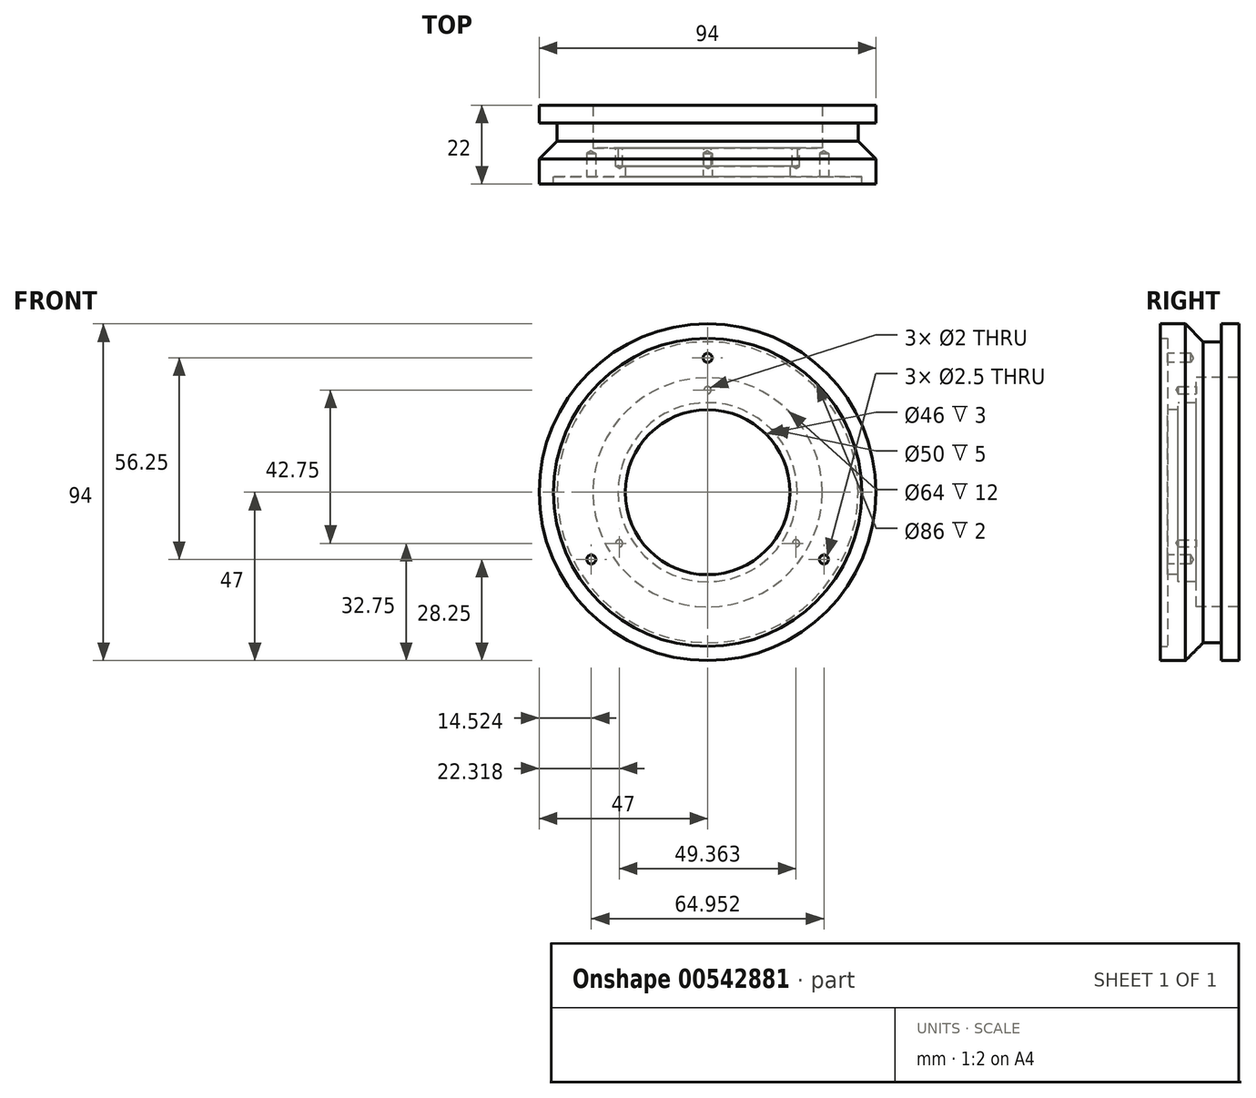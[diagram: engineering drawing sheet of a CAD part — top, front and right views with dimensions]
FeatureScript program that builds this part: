
annotation { "Feature Type Name" : "Feature", "Feature Type Description" : "" }
export const myFeature = defineFeature(function(context is Context, id is Id, definition is map)
    precondition{}
    {
        {
            var Q0;
            Q0=qCreatedBy(makeId("Right.planeOp"),FACE);
            var sketch = newSketch(context, id + "F0", { "sketchPlane" : qUnion([Q0])});
            skLineSegment(sketch, "E0", {"start": v(0, 47) * mm, "end": v(0, 23) * mm});
            skLineSegment(sketch, "E1", {"start": v(0, 23) * mm, "end": v(3, 23) * mm});
            skLineSegment(sketch, "E2", {"start": v(3, 23) * mm, "end": v(3, 25) * mm});
            skLineSegment(sketch, "E3", {"start": v(3, 25) * mm, "end": v(8, 25) * mm});
            skLineSegment(sketch, "E4", {"start": v(8, 25) * mm, "end": v(8, 32) * mm});
            skLineSegment(sketch, "E5", {"start": v(8, 32) * mm, "end": v(20, 32) * mm});
            skLineSegment(sketch, "E6", {"start": v(20, 32) * mm, "end": v(20, 47) * mm});
            skLineSegment(sketch, "E7", {"start": v(20, 47) * mm, "end": v(15, 47) * mm});
            skLineSegment(sketch, "E8", {"start": v(15, 47) * mm, "end": v(15, 42) * mm});
            skLineSegment(sketch, "E9", {"start": v(15, 42) * mm, "end": v(10, 42) * mm});
            skLineSegment(sketch, "E10", {"start": v(10, 42) * mm, "end": v(5, 47) * mm});
            skLineSegment(sketch, "E11", {"start": v(5, 47) * mm, "end": v(0, 47) * mm});
            skLineSegment(sketch, "E12", {"start": v(0, 0) * mm, "end": v(26.07, 0) * mm, "construction": true});
            skSolve(sketch);
        }
        {
            var Q0;
            Q0=makeQuery(id+"F0.imprint","IMPRINT",FACE,{"disambiguationData":[TD([[makeQuery(id+"F0.imprint","IMPRINT",EDGE,{"derivedFrom":sQuery(id+"F0.wireOp",EDGE,"E0")}),1.0]])]});
            var Q1;
            Q1=sQuery(id+"F0.wireOp",EDGE,"E12");
            revolve(context, id + "F1", {"entities" : qUnion([Q0]), "axis" : qUnion([Q1]), "revolveType" : RevolveType.FULL});
        }
        {
            var Q0;
            Q0=makeQuery(id+"F1.opRevolve","SWEPT_FACE",FACE,{"disambiguationData":[OSD([sQuery(id+"F0.wireOp",EDGE,"E4")])]});
            var sketch = newSketch(context, id + "F2", { "sketchPlane" : qUnion([Q0])});
            skLineSegment(sketch, "E13", {"start": v(0, 32) * mm, "end": v(0, 25) * mm, "construction": true});
            skPoint(sketch, "E14", {"position": v(0, 28.5) * mm});
            skPoint(sketch, "E15.1.0", {"position": v(-24.68, -14.25) * mm});
            skPoint(sketch, "E15.2.0", {"position": v(24.68, -14.25) * mm});
            skPoint(sketch, "E15.center", {"position": v(0, 0) * mm});
            skSolve(sketch);
        }
        {
            var Q0;
            Q0=sQuery(id+"F2.wireOp",VERTEX,"E14");
            var Q1;
            Q1=sQuery(id+"F2.wireOp",VERTEX,"E15.2.0");
            var Q2;
            Q2=sQuery(id+"F2.wireOp",VERTEX,"E15.1.0");
            var Q3;
            Q3=makeQuery(id+"F1.opRevolve","SWEPT_BODY",BODY,{"disambiguationData":[OSD([sQuery(id+"F0.wireOp",EDGE,"E0"),sQuery(id+"F0.wireOp",EDGE,"E1"),sQuery(id+"F0.wireOp",EDGE,"E2"),sQuery(id+"F0.wireOp",EDGE,"E3"),sQuery(id+"F0.wireOp",EDGE,"E4"),sQuery(id+"F0.wireOp",EDGE,"E5"),sQuery(id+"F0.wireOp",EDGE,"E6"),sQuery(id+"F0.wireOp",EDGE,"E7"),sQuery(id+"F0.wireOp",EDGE,"E8"),sQuery(id+"F0.wireOp",EDGE,"E9"),sQuery(id+"F0.wireOp",EDGE,"E10"),sQuery(id+"F0.wireOp",EDGE,"E11")])]});
            hole(context, id + "F3", {"style" : HoleStyle.SIMPLE, "endStyle" : HoleEndStyle.BLIND, "holeDiameter" : 2 * mm, "majorDiameter" : 3 * mm, "holeDepth" : 5 * mm, "isTappedThrough" : true, "tappedDepth" : 6.5 * mm, "tapClearance" : 3, "locations" : qUnion([Q0, Q1, Q2]), "scope" : qUnion([Q3])});
        }
        {
            var Q0;
            Q0=qCreatedBy(makeId("Right.planeOp"),FACE);
            var sketch = newSketch(context, id + "F4", { "sketchPlane" : qUnion([Q0])});
            skLineSegment(sketch, "E16", {"start": v(0, 47) * mm, "end": v(0, 43) * mm});
            skLineSegment(sketch, "E17", {"start": v(0, 43) * mm, "end": v(-2, 43) * mm});
            skLineSegment(sketch, "E18", {"start": v(-2, 43) * mm, "end": v(-2, 47) * mm});
            skLineSegment(sketch, "E19", {"start": v(-2, 47) * mm, "end": v(0, 47) * mm});
            skLineSegment(sketch, "E20", {"start": v(0, 0) * mm, "end": v(-15.8, 0) * mm, "construction": true});
            skSolve(sketch);
        }
        {
            var Q0;
            Q0=makeQuery(id+"F4.imprint","IMPRINT",FACE,{"disambiguationData":[TD([[makeQuery(id+"F4.imprint","IMPRINT",EDGE,{"derivedFrom":sQuery(id+"F4.wireOp",EDGE,"E16")}),-1.0]])]});
            var Q1;
            Q1=sQuery(id+"F4.wireOp",EDGE,"E20");
            revolve(context, id + "F5", {"operationType" : NewBodyOperationType.ADD, "entities" : qUnion([Q0]), "axis" : qUnion([Q1]), "revolveType" : RevolveType.FULL});
        }
        {
            var Q0;
            Q0=makeQuery(id+"F1.opRevolve","SWEPT_FACE",FACE,{"disambiguationData":[OSD([sQuery(id+"F0.wireOp",EDGE,"E0")])]});
            var sketch = newSketch(context, id + "F6", { "sketchPlane" : qUnion([Q0])});
            skCircle(sketch, "E21.0", {"center": v(0, 0) * mm, "radius": 32 * mm});
            skLineSegment(sketch, "E22", {"start": v(0, 32) * mm, "end": v(0, 43) * mm, "construction": true});
            skPoint(sketch, "E23", {"position": v(0, 37.5) * mm});
            skPoint(sketch, "E24.1.0", {"position": v(-32.48, -18.75) * mm});
            skPoint(sketch, "E24.2.0", {"position": v(32.48, -18.75) * mm});
            skSolve(sketch);
        }
        {
            var Q0;
            Q0=sQuery(id+"F6.wireOp",VERTEX,"E23");
            var Q1;
            Q1=sQuery(id+"F6.wireOp",VERTEX,"E24.2.0");
            var Q2;
            Q2=sQuery(id+"F6.wireOp",VERTEX,"E24.1.0");
            var Q3;
            Q3=makeQuery(id+"F1.opRevolve","SWEPT_BODY",BODY,{"disambiguationData":[OSD([sQuery(id+"F0.wireOp",EDGE,"E0"),sQuery(id+"F0.wireOp",EDGE,"E1"),sQuery(id+"F0.wireOp",EDGE,"E2"),sQuery(id+"F0.wireOp",EDGE,"E3"),sQuery(id+"F0.wireOp",EDGE,"E4"),sQuery(id+"F0.wireOp",EDGE,"E5"),sQuery(id+"F0.wireOp",EDGE,"E6"),sQuery(id+"F0.wireOp",EDGE,"E7"),sQuery(id+"F0.wireOp",EDGE,"E8"),sQuery(id+"F0.wireOp",EDGE,"E9"),sQuery(id+"F0.wireOp",EDGE,"E10"),sQuery(id+"F0.wireOp",EDGE,"E11")])]});
            hole(context, id + "F7", {"style" : HoleStyle.SIMPLE, "endStyle" : HoleEndStyle.BLIND, "standardTappedOrClearance" : lookupTablePath({ "standard" : "ISO", "engagement" : "75%", "pitch" : "0.5 mm", "size" : "M3", "type" : "Tapped" }), "standardBlindInLast" : lookupTablePath({ "standard" : "ISO", "engagement" : "75%", "pitch" : "0.5 mm", "size" : "M3", "type" : "Tapped" }), "holeDiameter" : 2.5 * mm, "majorDiameter" : 3 * mm, "showTappedDepth" : true, "holeDepth" : 6.5 * mm, "isTappedThrough" : true, "tappedDepth" : 5 * mm, "tapClearance" : 3, "locations" : qUnion([Q0, Q1, Q2]), "scope" : qUnion([Q3])});
        }
    });
